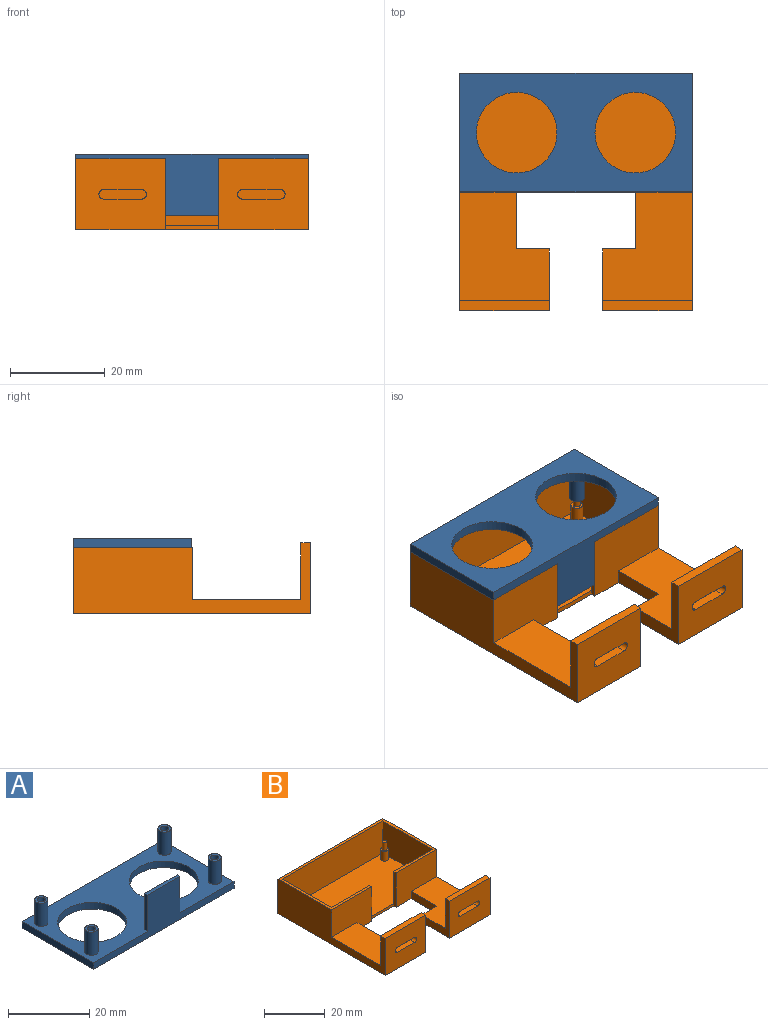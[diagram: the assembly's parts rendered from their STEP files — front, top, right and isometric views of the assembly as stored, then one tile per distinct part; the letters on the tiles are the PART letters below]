
ASSEMBLY  parts=2 mates=1
PART A: 28 faces, bbox 49x25x13 mm
  f0: plane 49x13mm, normal (0,-1,0), area 221.8mm2, adj f1,f3,f6,f7,f8,f10,f11
  f1: plane 25x2mm, normal (1,0,0), area 50mm2, adj f0,f2,f6,f7
  f2: plane 49x2mm, normal (0,1,0), area 98mm2, adj f1,f3,f6,f7
  f3: plane 25x2mm, normal (-1,0,0), area 50mm2, adj f0,f2,f6,f7
  f4: cylinder r=8.5mm len=17mm, axis (0,0,-1), area 106.8mm2, adj f6,f7
  f5: cylinder r=8.5mm len=17mm, axis (0,0,-1), area 106.8mm2, adj f6,f7
  f6: plane 49x25mm, normal (0,0,1), area 726.6mm2, adj f0,f1,f2,f3,f4,f5,f8,f9
  f7: plane 49x25mm, normal (0,0,-1), area 771mm2, adj f0,f1,f2,f3,f4,f5
  f8: plane 11x1mm, normal (1,0,0), area 11mm2, adj f0,f6,f9,f11
  f9: plane 11.25x11mm, normal (0,1,0), area 123.8mm2, adj f6,f8,f10,f11
  f10: plane 11x1mm, normal (-1,0,0), area 11mm2, adj f0,f6,f9,f11
  f11: plane 11.25x1mm, normal (0,0,1), area 11.2mm2, adj f0,f8,f9,f10
  f12: cylinder r=1mm len=2mm, axis (0,0,-1), area 9.4mm2, adj f14,f24
  f13: cylinder r=1.62mm len=7mm, axis (0,0,-1), area 71.5mm2, adj f6,f14
  f14: plane 3.25x3.25mm, normal (0,0,1), area 5.2mm2, adj f12,f13
  f15: cylinder r=1.62mm len=7mm, axis (0,0,-1), area 71.5mm2, adj f6,f17
  f16: cylinder r=1mm len=2mm, axis (0,0,-1), area 9.4mm2, adj f17,f25
  f17: plane 3.25x3.25mm, normal (0,0,1), area 5.2mm2, adj f15,f16
  f18: cylinder r=1.62mm len=7mm, axis (0,0,-1), area 71.5mm2, adj f6,f20
  f19: cylinder r=1mm len=2mm, axis (0,0,-1), area 9.4mm2, adj f20,f26
  f20: plane 3.25x3.25mm, normal (0,0,1), area 5.2mm2, adj f18,f19
  f21: cylinder r=1mm len=2mm, axis (0,0,-1), area 9.4mm2, adj f23,f27
  f22: cylinder r=1.62mm len=7mm, axis (0,0,-1), area 71.5mm2, adj f6,f23
  f23: plane 3.25x3.25mm, normal (0,0,1), area 5.2mm2, adj f21,f22
  f24: plane 2x2mm, normal (0,0,1), area 3.1mm2, adj f12
  f25: plane 2x2mm, normal (0,0,1), area 3.1mm2, adj f16
  f26: plane 2x2mm, normal (0,0,1), area 3.1mm2, adj f19
  f27: plane 2x2mm, normal (0,0,1), area 3.1mm2, adj f21
PART B: 54 faces, bbox 49x50x15 mm
  f0: plane 18.88x15mm, normal (0,-1,0), area 264mm2, adj f7,f30,f38,f45,f46,f47,f52,f53
  f1: plane 18.88x15mm, normal (0,-1,0), area 264mm2, adj f7,f32,f40,f44,f48,f49,f50,f51
  f2: plane 18.88x12mm, normal (0,1,0), area 207.4mm2, adj f32,f40,f43,f44,f48,f49,f50,f51
  f3: plane 18.88x12mm, normal (0,1,0), area 207.4mm2, adj f4,f30,f38,f45,f46,f47,f52,f53
  f4: plane 22.94x18.88mm, normal (0,0,1), area 349mm2, adj f3,f29,f30,f37,f38,f39
  f5: plane 11.25x1mm, normal (0,-1,0), area 11.2mm2, adj f6,f7,f34,f35
  f6: plane 47x23mm, normal (0,0,1), area 1061.4mm2, adj f5,f8,f12,f14,f16,f24,f25,f26
  f7: plane 50x49mm, normal (0,0,-1), area 1989.5mm2, adj f0,f1,f5,f29,f30,f31,f32,f33
  f8: cylinder r=1.25mm len=4mm, axis (0,0,-1), area 31.4mm2, adj f6,f9
  f9: plane 2.5x2.5mm, normal (0,0,1), area 3.1mm2, adj f8,f11
  f10: plane 1.5x1.5mm, normal (0,0,1), area 1.8mm2, adj f11
  f11: cylinder r=0.75mm len=3mm, axis (0,0,-1), area 14.1mm2, adj f9,f10
  f12: cylinder r=1.25mm len=4mm, axis (0,0,-1), area 31.4mm2, adj f6,f13
  f13: plane 2.5x2.5mm, normal (0,0,1), area 3.1mm2, adj f12,f19
  f14: cylinder r=1.25mm len=4mm, axis (0,0,-1), area 31.4mm2, adj f6,f15
  f15: plane 2.5x2.5mm, normal (0,0,1), area 3.1mm2, adj f14,f21
  f16: cylinder r=1.25mm len=4mm, axis (0,0,-1), area 31.4mm2, adj f6,f17
  f17: plane 2.5x2.5mm, normal (0,0,1), area 3.1mm2, adj f16,f23
  f18: plane 1.5x1.5mm, normal (0,0,1), area 1.8mm2, adj f19
  f19: cylinder r=0.75mm len=3mm, axis (0,0,-1), area 14.1mm2, adj f13,f18
  f20: plane 1.5x1.5mm, normal (0,0,1), area 1.8mm2, adj f21
  f21: cylinder r=0.75mm len=3mm, axis (0,0,-1), area 14.1mm2, adj f15,f20
  f22: plane 1.5x1.5mm, normal (0,0,1), area 1.8mm2, adj f23
  f23: cylinder r=0.75mm len=3mm, axis (0,0,-1), area 14.1mm2, adj f17,f22
  f24: plane 17.88x13mm, normal (0,1,0), area 232.4mm2, adj f6,f28,f34,f36
  f25: plane 17.88x13mm, normal (0,1,0), area 232.4mm2, adj f6,f26,f35,f36
  f26: plane 23x13mm, normal (-1,0,0), area 299mm2, adj f6,f25,f27,f36
  f27: plane 47x13mm, normal (0,-1,0), area 611mm2, adj f6,f26,f28,f36
  f28: plane 23x13mm, normal (1,0,0), area 299mm2, adj f6,f24,f27,f36
  f29: plane 18.88x14mm, normal (0,-1,0), area 228.6mm2, adj f4,f7,f30,f35,f36,f39
  f30: plane 50x15mm, normal (1,0,0), area 449.7mm2, adj f0,f3,f4,f7,f29,f31,f36,f45
  f31: plane 49x14mm, normal (0,1,0), area 686mm2, adj f7,f30,f32,f36
  f32: plane 50x15mm, normal (-1,0,0), area 449.7mm2, adj f1,f2,f7,f31,f33,f36,f43,f44
  f33: plane 18.88x14mm, normal (0,-1,0), area 228.6mm2, adj f7,f32,f34,f36,f42,f43
  f34: plane 14x1mm, normal (1,0,0), area 14mm2, adj f5,f7,f24,f33,f36
  f35: plane 14x1mm, normal (-1,0,0), area 14mm2, adj f5,f7,f25,f29,f36
  f36: plane 49x25mm, normal (0,0,1), area 132.8mm2, adj f24,f25,f26,f27,f28,f29,f30,f31
  f37: plane 7x3mm, normal (0,1,0), area 21mm2, adj f4,f7,f38,f39
  f38: plane 15x13mm, normal (-1,0,0), area 63.7mm2, adj f0,f3,f4,f7,f37,f45
  f39: plane 12x3mm, normal (-1,0,0), area 36mm2, adj f4,f7,f29,f37
  f40: plane 15x13mm, normal (1,0,0), area 63.7mm2, adj f1,f2,f7,f41,f43,f44
  f41: plane 7x3mm, normal (0,1,0), area 21mm2, adj f7,f40,f42,f43
  f42: plane 12x3mm, normal (1,0,0), area 36mm2, adj f7,f33,f41,f43
  f43: plane 22.94x18.88mm, normal (0,0,1), area 349mm2, adj f2,f32,f33,f40,f41,f42
  f44: plane 18.88x2.06mm, normal (0,0,1), area 38.8mm2, adj f1,f2,f32,f40
  f45: plane 18.88x2.06mm, normal (0,0,1), area 38.8mm2, adj f0,f3,f30,f38
  f46: plane 8x2.06mm, normal (0,0,1), area 16.5mm2, adj f0,f3,f52,f53
  f47: plane 8x2.06mm, normal (0,0,-1), area 16.5mm2, adj f0,f3,f52,f53
  f48: plane 8x2.06mm, normal (0,0,1), area 16.5mm2, adj f1,f2,f50,f51
  f49: plane 8x2.06mm, normal (0,0,-1), area 16.5mm2, adj f1,f2,f50,f51
  f50: cylinder r=1mm len=2.06mm, axis (0,1,0), area 6.5mm2, adj f1,f2,f48,f49
  f51: cylinder r=1mm len=2.06mm, axis (0,1,0), area 6.5mm2, adj f1,f2,f48,f49
  f52: cylinder r=1mm len=2.06mm, axis (0,1,0), area 6.5mm2, adj f0,f3,f46,f47
  f53: cylinder r=1mm len=2.06mm, axis (0,-1,0), area 6.5mm2, adj f0,f3,f46,f47
PLACE A rot(axis=(0,1,0),180deg) t=(-130.16,-57.54,-27.16)mm
PLACE B t=(-127.07,-50.09,-43.16)mm
MATE fastened A.f15 <-> B.f8  axis (0,0,-1) through (-188.66,-25.12,-36.16)mm
